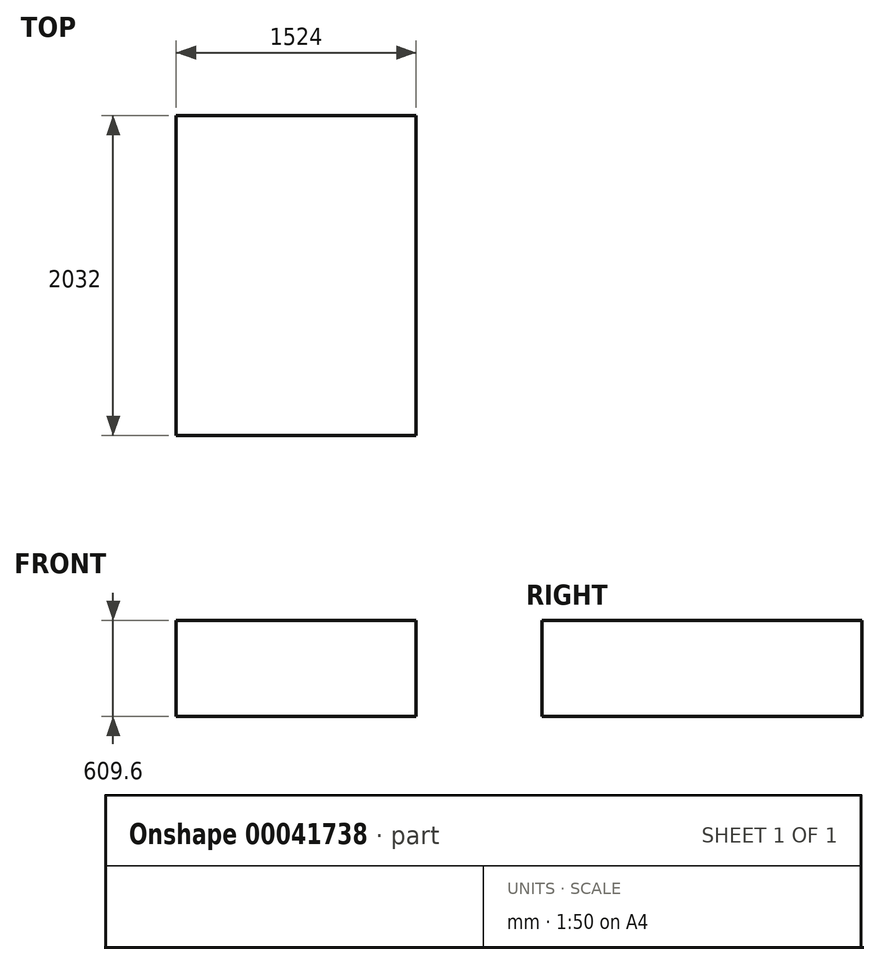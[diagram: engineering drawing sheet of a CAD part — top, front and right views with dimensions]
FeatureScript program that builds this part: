
annotation { "Feature Type Name" : "Feature", "Feature Type Description" : "" }
export const myFeature = defineFeature(function(context is Context, id is Id, definition is map)
    precondition{}
    {
        {
            var Q0;
            Q0=qCreatedBy(makeId("Top.planeOp"),FACE);
            var sketch = newSketch(context, id + "F0", { "sketchPlane" : qUnion([Q0])});
            skLineSegment(sketch, "E0.bottom", {"start": v(0, 0) * mm, "end": v(1524, 0) * mm});
            skLineSegment(sketch, "E0.top", {"start": v(0, -2032) * mm, "end": v(1524, -2032) * mm});
            skLineSegment(sketch, "E0.left", {"start": v(0, 0) * mm, "end": v(0, -2032) * mm});
            skLineSegment(sketch, "E0.right", {"start": v(1524, 0) * mm, "end": v(1524, -2032) * mm});
            skSolve(sketch);
        }
        {
            var Q0;
            Q0 = qSketchRegion(id + "F0", true);
            extrude(context, id + "F1", {"entities" : qUnion([Q0]), "depth" : 609.6 * mm, "offsetDistance" : 30.48 * mm});
        }
    });
